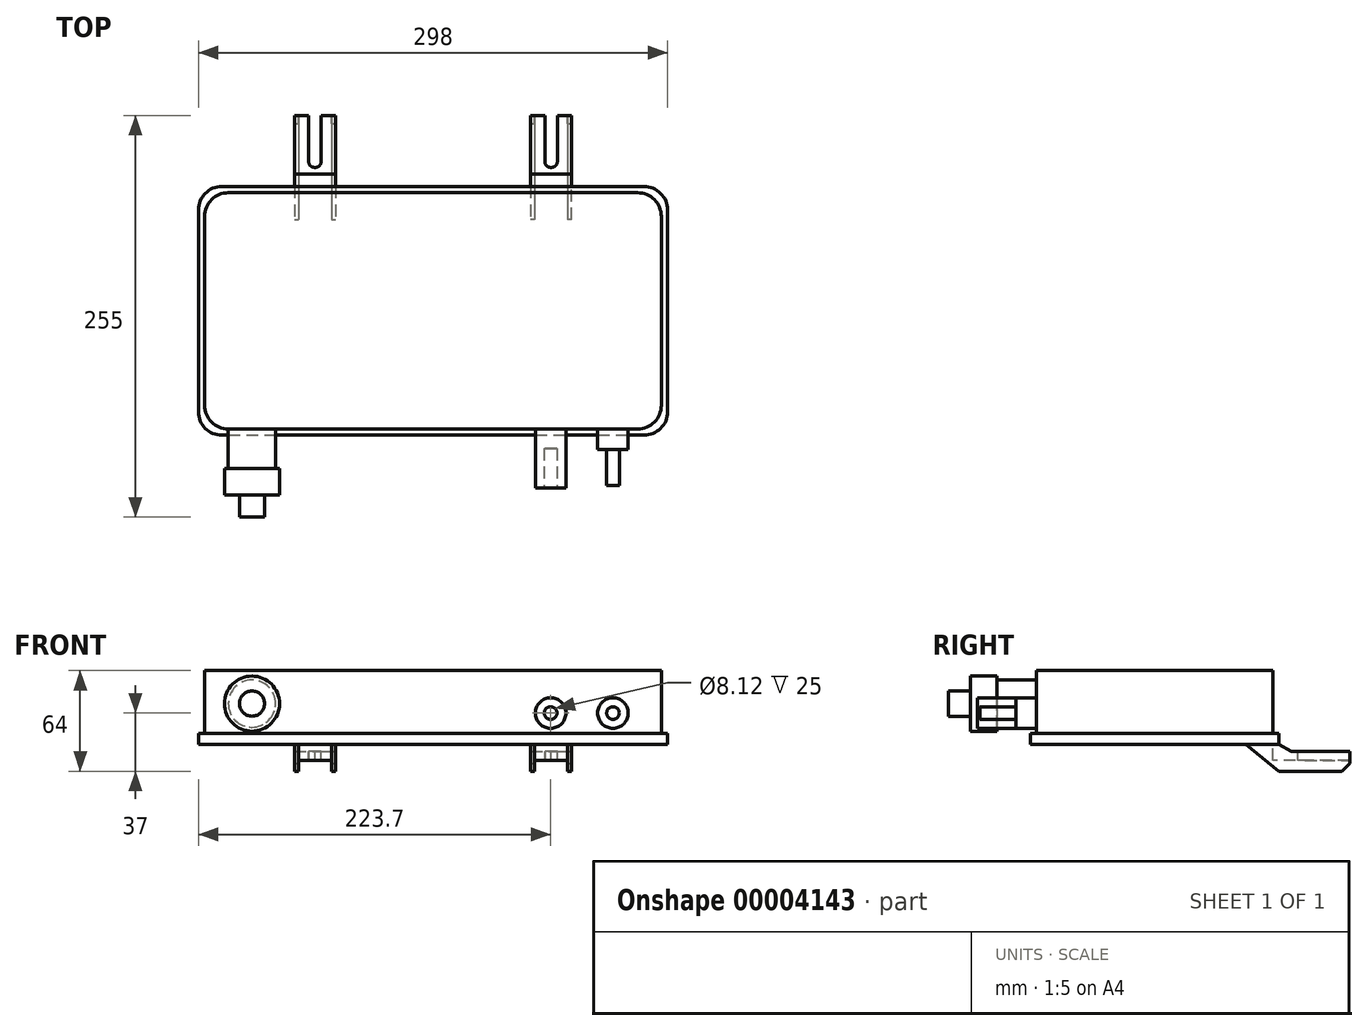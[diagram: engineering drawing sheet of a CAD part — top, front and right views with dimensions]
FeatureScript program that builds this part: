
annotation { "Feature Type Name" : "Feature", "Feature Type Description" : "" }
export const myFeature = defineFeature(function(context is Context, id is Id, definition is map)
    precondition{}
    {
        {
            var Q0;
            Q0=qCreatedBy(makeId("Top.planeOp"),FACE);
            var sketch = newSketch(context, id + "F0", { "sketchPlane" : qUnion([Q0])});
            skLineSegment(sketch, "E0.rect.bottom", {"start": v(145, -75) * mm, "end": v(-145, -75) * mm});
            skLineSegment(sketch, "E0.rect.top", {"start": v(145, 75) * mm, "end": v(-145, 75) * mm});
            skLineSegment(sketch, "E0.rect.left", {"start": v(145, -75) * mm, "end": v(145, 75) * mm});
            skLineSegment(sketch, "E0.rect.right", {"start": v(-145, -75) * mm, "end": v(-145, 75) * mm});
            skPoint(sketch, "E0.rect.middle", {"position": v(0, 0) * mm});
            skSolve(sketch);
        }
        {
            var Q0;
            Q0=makeQuery(id+"F0.imprint","IMPRINT",FACE,{"disambiguationData":[TD([[makeQuery(id+"F0.imprint","IMPRINT",EDGE,{"derivedFrom":sQuery(id+"F0.wireOp",EDGE,"E0.rect.bottom")}),-1.0]])]});
            extrude(context, id + "F1", {"entities" : qUnion([Q0]), "depth" : 40 * mm});
        }
        {
            var Q0;
            Q0=makeQuery(id+"F1.opExtrude","CAP_FACE",FACE,{"disambiguationData":[OSD([sQuery(id+"F0.wireOp",EDGE,"E0.rect.bottom"),sQuery(id+"F0.wireOp",EDGE,"E0.rect.top"),sQuery(id+"F0.wireOp",EDGE,"E0.rect.left"),sQuery(id+"F0.wireOp",EDGE,"E0.rect.right")])],"isStart":true});
            var sketch = newSketch(context, id + "F2", { "sketchPlane" : qUnion([Q0])});
            skLineSegment(sketch, "E1.rect.bottom", {"start": v(-149, 79) * mm, "end": v(149, 79) * mm});
            skLineSegment(sketch, "E1.rect.top", {"start": v(-149, -79) * mm, "end": v(149, -79) * mm});
            skLineSegment(sketch, "E1.rect.left", {"start": v(-149, 79) * mm, "end": v(-149, -79) * mm});
            skLineSegment(sketch, "E1.rect.right", {"start": v(149, 79) * mm, "end": v(149, -79) * mm});
            skPoint(sketch, "E1.rect.middle", {"position": v(0, 0) * mm});
            skSolve(sketch);
        }
        {
            var Q0;
            Q0=makeQuery(id+"F2.imprint","IMPRINT",FACE,{"disambiguationData":[TD([[makeQuery(id+"F2.imprint","IMPRINT",EDGE,{"derivedFrom":sQuery(id+"F2.wireOp",EDGE,"E1.rect.bottom")}),-1.0]])]});
            var Q1;
            Q1=makeQuery(id+"F2.imprint","IMPRINT",FACE,{"disambiguationData":[TD([[makeQuery(id+"F2.imprint","IMPRINT",EDGE,{"derivedFrom":makeQuery(id+"F1.opExtrude","CAP_EDGE",EDGE,{"disambiguationData":[OSD([sQuery(id+"F0.wireOp",EDGE,"E0.rect.bottom")])],"isStart":true})}),1.0]])]});
            extrude(context, id + "F3", {"entities" : qUnion([Q0, Q1]), "operationType" : NewBodyOperationType.ADD, "depth" : 7 * mm});
        }
        {
            var Q0;
            Q0=makeQuery(id+"F1.opExtrude","SWEPT_FACE",FACE,{"disambiguationData":[OSD([sQuery(id+"F0.wireOp",EDGE,"E0.rect.bottom")])]});
            var sketch = newSketch(context, id + "F4", { "sketchPlane" : qUnion([Q0])});
            skCircle(sketch, "E2", {"center": v(-115, 19) * mm, "radius": 15 * mm});
            skCircle(sketch, "E3", {"center": v(114.3, 13) * mm, "radius": 9.7 * mm});
            skCircle(sketch, "E4", {"center": v(74.7, 13) * mm, "radius": 9.7 * mm});
            skSolve(sketch);
        }
        {
            var Q0;
            Q0=makeQuery(id+"F4.imprint","IMPRINT",FACE,{"disambiguationData":[TD([[makeQuery(id+"F4.imprint","IMPRINT",EDGE,{"derivedFrom":sQuery(id+"F4.wireOp",EDGE,"E2")}),1.0]])]});
            extrude(context, id + "F5", {"entities" : qUnion([Q0]), "operationType" : NewBodyOperationType.ADD, "depth" : 25 * mm});
        }
        {
            var Q0;
            Q0=makeQuery(id+"F5.opExtrude","CAP_FACE",FACE,{"disambiguationData":[OSD([sQuery(id+"F4.wireOp",EDGE,"E2")])],"isStart":false});
            var sketch = newSketch(context, id + "F6", { "sketchPlane" : qUnion([Q0])});
            skCircle(sketch, "E5", {"center": v(-115, 19) * mm, "radius": 17.5 * mm});
            skSolve(sketch);
        }
        {
            var Q0;
            Q0=makeQuery(id+"F6.imprint","IMPRINT",FACE,{"disambiguationData":[TD([[makeQuery(id+"F6.imprint","IMPRINT",EDGE,{"derivedFrom":sQuery(id+"F6.wireOp",EDGE,"E5")}),1.0]])]});
            var Q1;
            Q1=makeQuery(id+"F6.imprint","IMPRINT",FACE,{"disambiguationData":[TD([[makeQuery(id+"F6.imprint","IMPRINT",EDGE,{"derivedFrom":makeQuery(id+"F5.opExtrude","CAP_EDGE",EDGE,{"disambiguationData":[OSD([sQuery(id+"F4.wireOp",EDGE,"E2")])],"isStart":false})}),1.0]])]});
            extrude(context, id + "F7", {"entities" : qUnion([Q0, Q1]), "operationType" : NewBodyOperationType.ADD, "depth" : 17 * mm});
        }
        {
            var Q0;
            Q0=makeQuery(id+"F7.opExtrude","CAP_FACE",FACE,{"disambiguationData":[OSD([sQuery(id+"F6.wireOp",EDGE,"E5")])],"isStart":false});
            var sketch = newSketch(context, id + "F8", { "sketchPlane" : qUnion([Q0])});
            skCircle(sketch, "E6", {"center": v(-115, 19) * mm, "radius": 8 * mm});
            skSolve(sketch);
        }
        {
            var Q0;
            Q0=makeQuery(id+"F8.imprint","IMPRINT",FACE,{"disambiguationData":[TD([[makeQuery(id+"F8.imprint","IMPRINT",EDGE,{"derivedFrom":sQuery(id+"F8.wireOp",EDGE,"E6")}),1.0]])]});
            extrude(context, id + "F9", {"entities" : qUnion([Q0]), "operationType" : NewBodyOperationType.ADD, "depth" : 14 * mm});
        }
        {
            var Q0;
            Q0=makeQuery(id+"F4.imprint","IMPRINT",FACE,{"disambiguationData":[TD([[makeQuery(id+"F4.imprint","IMPRINT",EDGE,{"derivedFrom":sQuery(id+"F4.wireOp",EDGE,"E4")}),1.0]])]});
            extrude(context, id + "F10", {"entities" : qUnion([Q0]), "operationType" : NewBodyOperationType.ADD, "depth" : 37.5 * mm});
        }
        {
            var Q0;
            Q0=makeQuery(id+"F4.imprint","IMPRINT",FACE,{"disambiguationData":[TD([[makeQuery(id+"F4.imprint","IMPRINT",EDGE,{"derivedFrom":sQuery(id+"F4.wireOp",EDGE,"E3")}),1.0]])]});
            extrude(context, id + "F11", {"entities" : qUnion([Q0]), "operationType" : NewBodyOperationType.ADD, "depth" : 13 * mm});
        }
        {
            var Q0;
            Q0=makeQuery(id+"F11.opExtrude","CAP_FACE",FACE,{"disambiguationData":[OSD([sQuery(id+"F4.wireOp",EDGE,"E3")])],"isStart":false});
            var sketch = newSketch(context, id + "F12", { "sketchPlane" : qUnion([Q0])});
            skCircle(sketch, "E7", {"center": v(114.3, 13) * mm, "radius": 4 * mm});
            skSolve(sketch);
        }
        {
            var Q0;
            Q0=makeQuery(id+"F12.imprint","IMPRINT",FACE,{"disambiguationData":[TD([[makeQuery(id+"F12.imprint","IMPRINT",EDGE,{"derivedFrom":sQuery(id+"F12.wireOp",EDGE,"E7")}),1.0]])]});
            extrude(context, id + "F13", {"entities" : qUnion([Q0]), "operationType" : NewBodyOperationType.ADD, "depth" : 23 * mm});
        }
        {
            var Q0;
            Q0=makeQuery(id+"F10.opExtrude","CAP_FACE",FACE,{"disambiguationData":[OSD([sQuery(id+"F4.wireOp",EDGE,"E4")])],"isStart":false});
            var sketch = newSketch(context, id + "F14", { "sketchPlane" : qUnion([Q0])});
            skCircle(sketch, "E8", {"center": v(74.7, 13) * mm, "radius": 4.06 * mm});
            skSolve(sketch);
        }
        {
            var Q0;
            Q0=makeQuery(id+"F14.imprint","IMPRINT",FACE,{"disambiguationData":[TD([[makeQuery(id+"F14.imprint","IMPRINT",EDGE,{"derivedFrom":sQuery(id+"F14.wireOp",EDGE,"E8")}),1.0]])]});
            extrude(context, id + "F15", {"entities" : qUnion([Q0]), "operationType" : NewBodyOperationType.REMOVE, "oppositeDirection" : true, "depth" : 25 * mm});
        }
        {
            var Q0;
            Q0=makeQuery(id+"F3.opExtrude","CAP_FACE",FACE,{"disambiguationData":[OSD([sQuery(id+"F2.wireOp",EDGE,"E1.rect.bottom"),sQuery(id+"F2.wireOp",EDGE,"E1.rect.top"),sQuery(id+"F2.wireOp",EDGE,"E1.rect.left"),sQuery(id+"F2.wireOp",EDGE,"E1.rect.right")])],"isStart":false});
            var sketch = newSketch(context, id + "F16", { "sketchPlane" : qUnion([Q0])});
            skLineSegment(sketch, "E9", {"start": v(88, -79) * mm, "end": v(88, -124) * mm});
            skLineSegment(sketch, "E10", {"start": v(88, -124) * mm, "end": v(79, -124) * mm});
            skLineSegment(sketch, "E11", {"start": v(79, -124) * mm, "end": v(79, -91) * mm});
            skLineSegment(sketch, "E12", {"start": v(79, -91) * mm, "end": v(71, -91) * mm});
            skLineSegment(sketch, "E13", {"start": v(71, -91) * mm, "end": v(71, -124) * mm});
            skLineSegment(sketch, "E14", {"start": v(71, -124) * mm, "end": v(62, -124) * mm});
            skLineSegment(sketch, "E15", {"start": v(62, -124) * mm, "end": v(62, -79) * mm});
            skLineSegment(sketch, "E16", {"start": v(85.5, -124) * mm, "end": v(85.5, -79) * mm});
            skLineSegment(sketch, "E17", {"start": v(64.5, -124) * mm, "end": v(64.5, -79) * mm});
            skLineSegment(sketch, "E18", {"start": v(85.5, -79) * mm, "end": v(85.5, -75) * mm});
            skLineSegment(sketch, "E19", {"start": v(85.5, -75) * mm, "end": v(64.5, -75) * mm});
            skLineSegment(sketch, "E20", {"start": v(64.5, -75) * mm, "end": v(64.5, -79) * mm});
            skLineSegment(sketch, "E21", {"start": v(88, -79) * mm, "end": v(88, -58) * mm});
            skLineSegment(sketch, "E22", {"start": v(88, -58) * mm, "end": v(85.5, -58) * mm});
            skLineSegment(sketch, "E23", {"start": v(85.5, -58) * mm, "end": v(85.5, -75) * mm});
            skLineSegment(sketch, "E24", {"start": v(64.5, -75) * mm, "end": v(64.5, -58) * mm});
            skLineSegment(sketch, "E25", {"start": v(64.5, -58) * mm, "end": v(62, -58) * mm});
            skLineSegment(sketch, "E26", {"start": v(62, -58) * mm, "end": v(62, -79) * mm});
            skLineSegment(sketch, "E27", {"start": v(0, 102) * mm, "end": v(0, -153.03) * mm, "construction": true});
            skLineSegment(sketch, "E28.0.MirrorCS", {"start": v(-85.5, -79) * mm, "end": v(-85.5, -75) * mm});
            skLineSegment(sketch, "E28.1.MirrorCS", {"start": v(-88, -58) * mm, "end": v(-85.5, -58) * mm});
            skLineSegment(sketch, "E28.2.MirrorCS", {"start": v(-64.5, -58) * mm, "end": v(-62, -58) * mm});
            skLineSegment(sketch, "E28.3.MirrorCS", {"start": v(-64.5, -75) * mm, "end": v(-64.5, -79) * mm});
            skLineSegment(sketch, "E28.4.MirrorCS", {"start": v(-71, -124) * mm, "end": v(-62, -124) * mm});
            skLineSegment(sketch, "E28.5.MirrorCS", {"start": v(-88, -124) * mm, "end": v(-79, -124) * mm});
            skLineSegment(sketch, "E28.6.MirrorCS", {"start": v(-85.5, -124) * mm, "end": v(-85.5, -79) * mm});
            skLineSegment(sketch, "E28.7.MirrorCS", {"start": v(-64.5, -75) * mm, "end": v(-64.5, -58) * mm});
            skLineSegment(sketch, "E28.8.MirrorCS", {"start": v(-64.5, -124) * mm, "end": v(-64.5, -79) * mm});
            skLineSegment(sketch, "E28.9.MirrorCS", {"start": v(-85.5, -75) * mm, "end": v(-64.5, -75) * mm});
            skLineSegment(sketch, "E28.10.MirrorCS", {"start": v(-62, -124) * mm, "end": v(-62, -79) * mm});
            skLineSegment(sketch, "E28.11.MirrorCS", {"start": v(-71, -91) * mm, "end": v(-71, -124) * mm});
            skLineSegment(sketch, "E28.12.MirrorCS", {"start": v(-88, -79) * mm, "end": v(-88, -124) * mm});
            skLineSegment(sketch, "E28.13.MirrorCS", {"start": v(-79, -91) * mm, "end": v(-71, -91) * mm});
            skLineSegment(sketch, "E28.14.MirrorCS", {"start": v(-62, -58) * mm, "end": v(-62, -79) * mm});
            skLineSegment(sketch, "E28.15.MirrorCS", {"start": v(-85.5, -58) * mm, "end": v(-85.5, -75) * mm});
            skLineSegment(sketch, "E28.16.MirrorCS", {"start": v(-88, -79) * mm, "end": v(-88, -58) * mm});
            skLineSegment(sketch, "E28.17.MirrorCS", {"start": v(-79, -124) * mm, "end": v(-79, -91) * mm});
            skSolve(sketch);
        }
        {
            var Q0;
            {var subQ2=sQuery(id+"F16.wireOp",EDGE,"E9");Q0=makeQuery(id+"F16.imprint","IMPRINT",FACE,{"disambiguationData":[TD([[makeQuery(id+"F16.imprint","IMPRINT",EDGE,{"derivedFrom":subQ2}),-1.0]])]});}
            var Q1;
            {var subQ2=sQuery(id+"F16.wireOp",EDGE,"E15");Q1=makeQuery(id+"F16.imprint","IMPRINT",FACE,{"disambiguationData":[TD([[makeQuery(id+"F16.imprint","IMPRINT",EDGE,{"derivedFrom":subQ2}),-1.0]])]});}
            var Q2;
            {var subQ1=sQuery(id+"F16.wireOp",EDGE,"E18");Q2=makeQuery(id+"F16.imprint","IMPRINT",FACE,{"disambiguationData":[TD([[makeQuery(id+"F16.imprint","IMPRINT",EDGE,{"derivedFrom":subQ1}),-1.0]])]});}
            var Q3;
            {var subQ1=sQuery(id+"F16.wireOp",EDGE,"E20");Q3=makeQuery(id+"F16.imprint","IMPRINT",FACE,{"disambiguationData":[TD([[makeQuery(id+"F16.imprint","IMPRINT",EDGE,{"derivedFrom":subQ1}),-1.0]])]});}
            var Q4;
            {var subQ2=sQuery(id+"F16.wireOp",EDGE,"E28.8.MirrorCS");Q4=makeQuery(id+"F16.imprint","IMPRINT",FACE,{"disambiguationData":[TD([[makeQuery(id+"F16.imprint","IMPRINT",EDGE,{"derivedFrom":subQ2}),-1.0]])]});}
            var Q5;
            Q5=makeQuery(id+"F16.imprint","IMPRINT",FACE,{"disambiguationData":[TD([[makeQuery(id+"F16.imprint","IMPRINT",EDGE,{"derivedFrom":sQuery(id+"F16.wireOp",EDGE,"E28.2.MirrorCS")}),-1.0]])]});
            var Q6;
            {var subQ2=sQuery(id+"F16.wireOp",EDGE,"E28.0.MirrorCS");Q6=makeQuery(id+"F16.imprint","IMPRINT",FACE,{"disambiguationData":[TD([[makeQuery(id+"F16.imprint","IMPRINT",EDGE,{"derivedFrom":subQ2}),1.0]])]});}
            var Q7;
            {var subQ2=sQuery(id+"F16.wireOp",EDGE,"E28.6.MirrorCS");Q7=makeQuery(id+"F16.imprint","IMPRINT",FACE,{"disambiguationData":[TD([[makeQuery(id+"F16.imprint","IMPRINT",EDGE,{"derivedFrom":subQ2}),1.0]])]});}
            extrude(context, id + "F17", {"entities" : qUnion([Q0, Q1, Q2, Q3, Q4, Q5, Q6, Q7]), "operationType" : NewBodyOperationType.ADD, "depth" : 17 * mm});
        }
        {
            var Q0;
            {var subQ5=sQuery(id+"F16.wireOp",EDGE,"E11");Q0=makeQuery(id+"F16.imprint","IMPRINT",FACE,{"disambiguationData":[TD([[makeQuery(id+"F16.imprint","IMPRINT",EDGE,{"derivedFrom":subQ5}),-1.0]])]});}
            var Q1;
            {var subQ2=sQuery(id+"F16.wireOp",EDGE,"E18");Q1=makeQuery(id+"F16.imprint","IMPRINT",FACE,{"disambiguationData":[TD([[makeQuery(id+"F16.imprint","IMPRINT",EDGE,{"derivedFrom":subQ2}),1.0]])]});}
            var Q2;
            {var subQ2=sQuery(id+"F16.wireOp",EDGE,"E28.6.MirrorCS");Q2=makeQuery(id+"F16.imprint","IMPRINT",FACE,{"disambiguationData":[TD([[makeQuery(id+"F16.imprint","IMPRINT",EDGE,{"derivedFrom":subQ2}),-1.0]])]});}
            var Q3;
            {var subQ2=sQuery(id+"F16.wireOp",EDGE,"E28.0.MirrorCS");Q3=makeQuery(id+"F16.imprint","IMPRINT",FACE,{"disambiguationData":[TD([[makeQuery(id+"F16.imprint","IMPRINT",EDGE,{"derivedFrom":subQ2}),-1.0]])]});}
            extrude(context, id + "F18", {"entities" : qUnion([Q0, Q1, Q2, Q3]), "operationType" : NewBodyOperationType.ADD, "depth" : 10 * mm});
        }
        {
            var Q0;
            Q0=makeQuery(id+"F17.opExtrude","SWEPT_FACE",FACE,{"disambiguationData":[OSD([sQuery(id+"F16.wireOp",EDGE,"E9"),sQuery(id+"F16.wireOp",EDGE,"E21")])]});
            var sketch = newSketch(context, id + "F19", { "sketchPlane" : qUnion([Q0])});
            skLineSegment(sketch, "E29", {"start": v(124, -11.5) * mm, "end": v(87, -11.5) * mm});
            skLineSegment(sketch, "E30", {"start": v(87, -11.5) * mm, "end": v(79, -7) * mm});
            skLineSegment(sketch, "E31", {"start": v(58, -7) * mm, "end": v(79, -24) * mm});
            skLineSegment(sketch, "E32", {"start": v(58, -7) * mm, "end": v(58, -24) * mm});
            skLineSegment(sketch, "E33", {"start": v(58, -24) * mm, "end": v(79, -24) * mm});
            skLineSegment(sketch, "E34", {"start": v(79, -7) * mm, "end": v(124, -7) * mm});
            skLineSegment(sketch, "E35", {"start": v(124, -7) * mm, "end": v(124, -11.5) * mm});
            skLineSegment(sketch, "E36", {"start": v(124, -19) * mm, "end": v(119, -24) * mm});
            skLineSegment(sketch, "E37", {"start": v(119, -24) * mm, "end": v(124, -24) * mm});
            skLineSegment(sketch, "E38", {"start": v(124, -24) * mm, "end": v(124, -19) * mm});
            skSolve(sketch);
        }
        {
            var Q0;
            Q0=makeQuery(id+"F19.imprint","IMPRINT",FACE,{"disambiguationData":[TD([[makeQuery(id+"F19.imprint","IMPRINT",EDGE,{"derivedFrom":sQuery(id+"F19.wireOp",EDGE,"E31")}),-1.0]])]});
            var Q1;
            Q1=makeQuery(id+"F19.imprint","IMPRINT",FACE,{"disambiguationData":[TD([[makeQuery(id+"F19.imprint","IMPRINT",EDGE,{"derivedFrom":sQuery(id+"F19.wireOp",EDGE,"E36")}),1.0]])]});
            var Q2;
            Q2=makeQuery(id+"F19.imprint","IMPRINT",FACE,{"disambiguationData":[TD([[makeQuery(id+"F19.imprint","IMPRINT",EDGE,{"derivedFrom":sQuery(id+"F19.wireOp",EDGE,"E29")}),-1.0]])]});
            extrude(context, id + "F20", {"entities" : qUnion([Q0, Q1, Q2]), "operationType" : NewBodyOperationType.REMOVE, "endBound" : BoundingType.THROUGH_ALL, "oppositeDirection" : true, "depth" : 25 * mm});
        }
        {
            var Q0;
            Q0=makeQuery(id+"F18.opExtrude","SWEPT_EDGE",EDGE,{"disambiguationData":[OSD([sQuery(id+"F16.wireOp",EDGE,"E11"),sQuery(id+"F16.wireOp",EDGE,"E12")])]});
            var Q1;
            Q1=makeQuery(id+"F18.opExtrude","SWEPT_EDGE",EDGE,{"disambiguationData":[OSD([sQuery(id+"F16.wireOp",EDGE,"E12"),sQuery(id+"F16.wireOp",EDGE,"E13")])]});
            var Q2;
            Q2=makeQuery(id+"F18.opExtrude","SWEPT_EDGE",EDGE,{"disambiguationData":[OSD([sQuery(id+"F16.wireOp",EDGE,"E28.11.MirrorCS"),sQuery(id+"F16.wireOp",EDGE,"E28.13.MirrorCS")])]});
            var Q3;
            Q3=makeQuery(id+"F18.opExtrude","SWEPT_EDGE",EDGE,{"disambiguationData":[OSD([sQuery(id+"F16.wireOp",EDGE,"E28.13.MirrorCS"),sQuery(id+"F16.wireOp",EDGE,"E28.17.MirrorCS")])]});
            fillet(context, id + "F21", {"entities" : qUnion([Q0, Q1, Q2, Q3]), "radius" : 4.5 * mm, "tangentPropagation" : true, "rho" : 0.5, "crossSection" : FilletCrossSection.CONIC, "allowEdgeOverflow" : false});
        }
        {
            var Q0;
            Q0=makeQuery(id+"F3.opExtrude","SWEPT_EDGE",EDGE,{"disambiguationData":[OSD([sQuery(id+"F2.wireOp",EDGE,"E1.rect.top"),sQuery(id+"F2.wireOp",EDGE,"E1.rect.left")])]});
            var Q1;
            Q1=makeQuery(id+"F1.opExtrude","SWEPT_EDGE",EDGE,{"disambiguationData":[OSD([sQuery(id+"F0.wireOp",EDGE,"E0.rect.top"),sQuery(id+"F0.wireOp",EDGE,"E0.rect.right")])]});
            var Q2;
            Q2=makeQuery(id+"F1.opExtrude","SWEPT_EDGE",EDGE,{"disambiguationData":[OSD([sQuery(id+"F0.wireOp",EDGE,"E0.rect.bottom"),sQuery(id+"F0.wireOp",EDGE,"E0.rect.right")])]});
            var Q3;
            Q3=makeQuery(id+"F3.opExtrude","SWEPT_EDGE",EDGE,{"disambiguationData":[OSD([sQuery(id+"F2.wireOp",EDGE,"E1.rect.bottom"),sQuery(id+"F2.wireOp",EDGE,"E1.rect.left")])]});
            var Q4;
            Q4=makeQuery(id+"F1.opExtrude","SWEPT_EDGE",EDGE,{"disambiguationData":[OSD([sQuery(id+"F0.wireOp",EDGE,"E0.rect.bottom"),sQuery(id+"F0.wireOp",EDGE,"E0.rect.left")])]});
            var Q5;
            Q5=makeQuery(id+"F3.opExtrude","SWEPT_EDGE",EDGE,{"disambiguationData":[OSD([sQuery(id+"F2.wireOp",EDGE,"E1.rect.bottom"),sQuery(id+"F2.wireOp",EDGE,"E1.rect.right")])]});
            var Q6;
            Q6=makeQuery(id+"F1.opExtrude","SWEPT_EDGE",EDGE,{"disambiguationData":[OSD([sQuery(id+"F0.wireOp",EDGE,"E0.rect.top"),sQuery(id+"F0.wireOp",EDGE,"E0.rect.left")])]});
            var Q7;
            Q7=makeQuery(id+"F3.opExtrude","SWEPT_EDGE",EDGE,{"disambiguationData":[OSD([sQuery(id+"F2.wireOp",EDGE,"E1.rect.top"),sQuery(id+"F2.wireOp",EDGE,"E1.rect.right")])]});
            fillet(context, id + "F22", {"entities" : qUnion([Q0, Q1, Q2, Q3, Q4, Q5, Q6, Q7]), "radius" : 15 * mm, "tangentPropagation" : true, "allowEdgeOverflow" : false});
        }
    });
